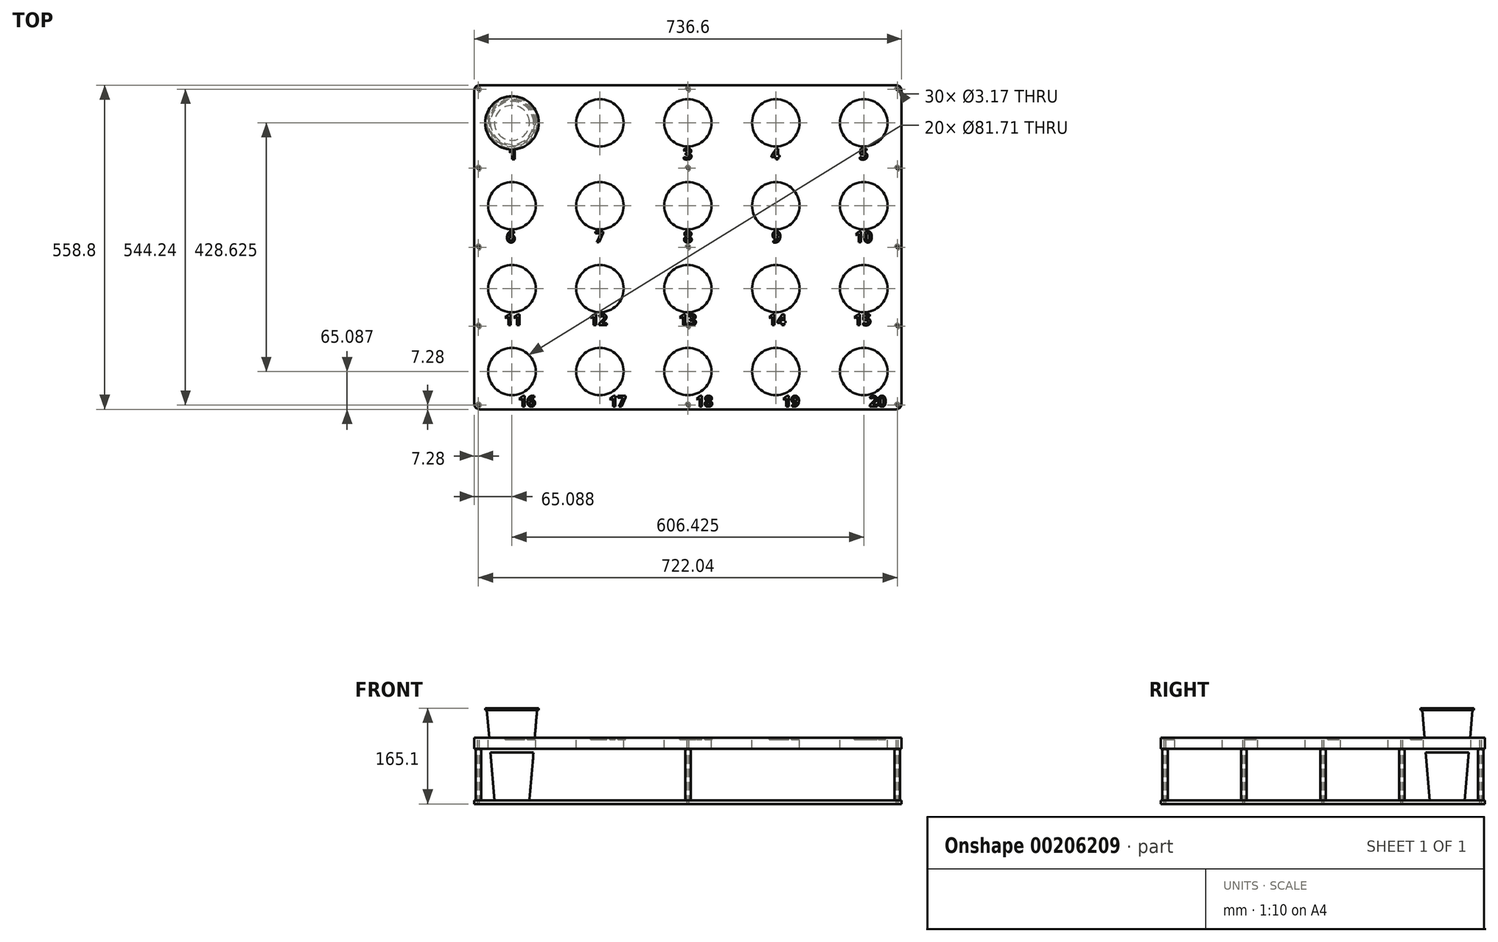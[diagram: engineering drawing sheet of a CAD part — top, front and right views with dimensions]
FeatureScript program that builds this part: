
annotation { "Feature Type Name" : "Feature", "Feature Type Description" : "" }
export const myFeature = defineFeature(function(context is Context, id is Id, definition is map)
    precondition{}
    {
        {
            var Q0;
            Q0=qCreatedBy(makeId("Top.planeOp"),FACE);
            var sketch = newSketch(context, id + "F0", { "sketchPlane" : qUnion([Q0])});
            skLineSegment(sketch, "E0.bottom", {"start": v(368.3, -279.4) * mm, "end": v(-368.3, -279.4) * mm});
            skLineSegment(sketch, "E0.top", {"start": v(368.3, 279.4) * mm, "end": v(-368.3, 279.4) * mm});
            skLineSegment(sketch, "E0.left", {"start": v(368.3, -279.4) * mm, "end": v(368.3, 279.4) * mm});
            skLineSegment(sketch, "E0.right", {"start": v(-368.3, -279.4) * mm, "end": v(-368.3, 279.4) * mm});
            skPoint(sketch, "E0.middle", {"position": v(0, 0) * mm});
            skSolve(sketch);
        }
        {
            var Q0;
            Q0 = qSketchRegion(id + "F0", true);
            extrude(context, id + "F1", {"entities" : qUnion([Q0]), "oppositeDirection" : true, "depth" : 19.05 * mm});
        }
        {
            var Q0;
            Q0=makeQuery(id+"F1.opExtrude","SWEPT_EDGE",EDGE,{"disambiguationData":[OSD([sQuery(id+"F0.wireOp",EDGE,"E0.bottom"),sQuery(id+"F0.wireOp",EDGE,"E0.right")])]});
            var Q1;
            Q1=makeQuery(id+"F1.opExtrude","SWEPT_EDGE",EDGE,{"disambiguationData":[OSD([sQuery(id+"F0.wireOp",EDGE,"E0.bottom"),sQuery(id+"F0.wireOp",EDGE,"E0.left")])]});
            var Q2;
            Q2=makeQuery(id+"F1.opExtrude","SWEPT_EDGE",EDGE,{"disambiguationData":[OSD([sQuery(id+"F0.wireOp",EDGE,"E0.top"),sQuery(id+"F0.wireOp",EDGE,"E0.left")])]});
            var Q3;
            Q3=makeQuery(id+"F1.opExtrude","SWEPT_EDGE",EDGE,{"disambiguationData":[OSD([sQuery(id+"F0.wireOp",EDGE,"E0.top"),sQuery(id+"F0.wireOp",EDGE,"E0.right")])]});
            fillet(context, id + "F2", {"entities" : qUnion([Q0, Q1, Q2, Q3]), "radius" : 9.52 * mm, "tangentPropagation" : true, "allowEdgeOverflow" : false});
        }
        {
            var Q0;
            Q0=makeQuery(id+"F1.opExtrude","CAP_FACE",FACE,{"disambiguationData":[OSD([sQuery(id+"F0.wireOp",EDGE,"E0.bottom"),sQuery(id+"F0.wireOp",EDGE,"E0.top"),sQuery(id+"F0.wireOp",EDGE,"E0.left"),sQuery(id+"F0.wireOp",EDGE,"E0.right")])],"isStart":false});
            var sketch = newSketch(context, id + "F3", { "sketchPlane" : qUnion([Q0])});
            skCircle(sketch, "E1", {"center": v(-361.02, 272.12) * mm, "radius": 4.76 * mm});
            skCircle(sketch, "E2", {"center": v(-361.02, 272.12) * mm, "radius": 6.35 * mm, "construction": true});
            skLineSegment(sketch, "E3", {"start": v(-361.02, 272.12) * mm, "end": v(-368.3, 272.12) * mm, "construction": true});
            skLineSegment(sketch, "E4", {"start": v(-361.02, 272.12) * mm, "end": v(-361.02, 279.4) * mm, "construction": true});
            skLineSegment(sketch, "E5", {"start": v(0, 0) * mm, "end": v(-361.02, 0) * mm, "construction": true});
            skLineSegment(sketch, "E6", {"start": v(0, 0) * mm, "end": v(0, 189.11) * mm, "construction": true});
            skLineSegment(sketch, "E7", {"start": v(-361.02, 272.12) * mm, "end": v(-361.02, 136.06) * mm, "construction": true});
            skLineSegment(sketch, "E8", {"start": v(-361.02, 136.06) * mm, "end": v(-361.02, 0) * mm, "construction": true});
            skCircle(sketch, "E9", {"center": v(-361.02, 136.06) * mm, "radius": 4.76 * mm});
            skCircle(sketch, "E10", {"center": v(-361.02, 0) * mm, "radius": 4.76 * mm});
            skCircle(sketch, "E11.MirrorC", {"center": v(-361.02, -136.06) * mm, "radius": 4.76 * mm});
            skCircle(sketch, "E12.MirrorC", {"center": v(-361.02, -272.12) * mm, "radius": 4.76 * mm});
            skCircle(sketch, "E13.MirrorC", {"center": v(361.02, -272.12) * mm, "radius": 4.76 * mm});
            skCircle(sketch, "E14.MirrorC", {"center": v(361.02, -136.06) * mm, "radius": 4.76 * mm});
            skCircle(sketch, "E15.MirrorC", {"center": v(361.02, 0) * mm, "radius": 4.76 * mm});
            skCircle(sketch, "E16.MirrorC", {"center": v(361.02, 136.06) * mm, "radius": 4.76 * mm});
            skCircle(sketch, "E17.MirrorC", {"center": v(361.02, 272.12) * mm, "radius": 4.76 * mm});
            skCircle(sketch, "E18.1.0.0", {"center": v(0, 272.12) * mm, "radius": 4.76 * mm});
            skCircle(sketch, "E18.1.0.1", {"center": v(0, 136.06) * mm, "radius": 4.76 * mm});
            skCircle(sketch, "E18.1.0.2", {"center": v(0, 0) * mm, "radius": 4.76 * mm});
            skCircle(sketch, "E18.1.0.3", {"center": v(0, -136.06) * mm, "radius": 4.76 * mm});
            skCircle(sketch, "E18.1.0.4", {"center": v(0, -272.12) * mm, "radius": 4.76 * mm});
            skLineSegment(sketch, "E18.direction1", {"start": v(-361.02, 272.12) * mm, "end": v(0, 272.12) * mm, "construction": true});
            skSolve(sketch);
        }
        {
            var Q0;
            Q0 = qSketchRegion(id + "F3", true);
            extrude(context, id + "F4", {"entities" : qUnion([Q0]), "depth" : 88.9 * mm});
        }
        {
            var Q0;
            Q0=makeQuery(id+"F4.opExtrude","CAP_FACE",FACE,{"disambiguationData":[OSD([sQuery(id+"F3.wireOp",EDGE,"E12.MirrorC")])],"isStart":false});
            var sketch = newSketch(context, id + "F5", { "sketchPlane" : qUnion([Q0])});
            skLineSegment(sketch, "E19.0.0", {"start": v(-358.78, 279.4) * mm, "end": v(358.77, 279.4) * mm});
            skArc(sketch, "E19.0.1", {"start": v(358.77, 279.4) * mm, "mid": v(365.51, 276.61) * mm, "end": v(368.3, 269.88) * mm});
            skLineSegment(sketch, "E19.0.2", {"start": v(368.3, 269.88) * mm, "end": v(368.3, -269.88) * mm});
            skArc(sketch, "E19.0.3", {"start": v(368.3, -269.88) * mm, "mid": v(365.51, -276.61) * mm, "end": v(358.78, -279.4) * mm});
            skLineSegment(sketch, "E19.0.4", {"start": v(358.78, -279.4) * mm, "end": v(-358.77, -279.4) * mm});
            skArc(sketch, "E19.0.5", {"start": v(-358.77, -279.4) * mm, "mid": v(-365.51, -276.61) * mm, "end": v(-368.3, -269.88) * mm});
            skLineSegment(sketch, "E19.0.6", {"start": v(-368.3, -269.88) * mm, "end": v(-368.3, 269.88) * mm});
            skArc(sketch, "E19.0.7", {"start": v(-368.3, 269.88) * mm, "mid": v(-365.51, 276.61) * mm, "end": v(-358.78, 279.4) * mm});
            skSolve(sketch);
        }
        {
            var Q0;
            Q0 = qSketchRegion(id + "F5", true);
            extrude(context, id + "F6", {"entities" : qUnion([Q0]), "operationType" : NewBodyOperationType.ADD, "depth" : 6.35 * mm});
        }
        {
            var Q0;
            Q0=makeQuery(id+"F1.opExtrude","CAP_FACE",FACE,{"disambiguationData":[OSD([sQuery(id+"F0.wireOp",EDGE,"E0.bottom"),sQuery(id+"F0.wireOp",EDGE,"E0.top"),sQuery(id+"F0.wireOp",EDGE,"E0.left"),sQuery(id+"F0.wireOp",EDGE,"E0.right")])],"isStart":true});
            var sketch = newSketch(context, id + "F7", { "sketchPlane" : qUnion([Q0])});
            skCircle(sketch, "E20", {"center": v(-303.21, 214.31) * mm, "radius": 46.04 * mm});
            skCircle(sketch, "E21.0.1.0", {"center": v(-303.21, 71.44) * mm, "radius": 46.04 * mm});
            skCircle(sketch, "E21.0.2.0", {"center": v(-303.21, -71.44) * mm, "radius": 46.04 * mm});
            skCircle(sketch, "E21.0.3.0", {"center": v(-303.21, -214.31) * mm, "radius": 46.04 * mm});
            skCircle(sketch, "E21.1.0.0", {"center": v(-151.6, 214.31) * mm, "radius": 46.04 * mm});
            skCircle(sketch, "E21.1.1.0", {"center": v(-151.6, 71.44) * mm, "radius": 46.04 * mm});
            skCircle(sketch, "E21.1.2.0", {"center": v(-151.6, -71.44) * mm, "radius": 46.04 * mm});
            skCircle(sketch, "E21.1.3.0", {"center": v(-151.6, -214.31) * mm, "radius": 46.04 * mm});
            skCircle(sketch, "E21.2.0.0", {"center": v(0, 214.31) * mm, "radius": 46.04 * mm});
            skCircle(sketch, "E21.2.1.0", {"center": v(0, 71.44) * mm, "radius": 46.04 * mm});
            skCircle(sketch, "E21.2.2.0", {"center": v(0, -71.44) * mm, "radius": 46.04 * mm});
            skCircle(sketch, "E21.2.3.0", {"center": v(0, -214.31) * mm, "radius": 46.04 * mm});
            skCircle(sketch, "E21.3.0.0", {"center": v(151.6, 214.31) * mm, "radius": 46.04 * mm});
            skCircle(sketch, "E21.3.1.0", {"center": v(151.6, 71.44) * mm, "radius": 46.04 * mm});
            skCircle(sketch, "E21.3.2.0", {"center": v(151.6, -71.44) * mm, "radius": 46.04 * mm});
            skCircle(sketch, "E21.3.3.0", {"center": v(151.6, -214.31) * mm, "radius": 46.04 * mm});
            skCircle(sketch, "E21.4.0.0", {"center": v(303.21, 214.31) * mm, "radius": 46.04 * mm});
            skCircle(sketch, "E21.4.1.0", {"center": v(303.21, 71.44) * mm, "radius": 46.04 * mm});
            skCircle(sketch, "E21.4.2.0", {"center": v(303.21, -71.44) * mm, "radius": 46.04 * mm});
            skCircle(sketch, "E21.4.3.0", {"center": v(303.21, -214.31) * mm, "radius": 46.04 * mm});
            skLineSegment(sketch, "E21.direction1", {"start": v(-303.21, 214.31) * mm, "end": v(-151.6, 214.31) * mm, "construction": true});
            skLineSegment(sketch, "E21.direction2", {"start": v(-303.21, 71.44) * mm, "end": v(-303.21, 214.31) * mm, "construction": true});
            skSolve(sketch);
        }
        {
            var Q0;
            Q0=makeQuery(id+"F6.opExtrude","CAP_FACE",FACE,{"disambiguationData":[OSD([sQuery(id+"F5.wireOp",EDGE,"E19.0.0"),sQuery(id+"F5.wireOp",EDGE,"E19.0.1"),sQuery(id+"F5.wireOp",EDGE,"E19.0.2"),sQuery(id+"F5.wireOp",EDGE,"E19.0.3"),sQuery(id+"F5.wireOp",EDGE,"E19.0.4"),sQuery(id+"F5.wireOp",EDGE,"E19.0.5"),sQuery(id+"F5.wireOp",EDGE,"E19.0.6"),sQuery(id+"F5.wireOp",EDGE,"E19.0.7")])],"isStart":true});
            var sketch = newSketch(context, id + "F8", { "sketchPlane" : qUnion([Q0])});
            skCircle(sketch, "E22", {"center": v(-303.21, 214.31) * mm, "radius": 30.16 * mm});
            skSolve(sketch);
        }
        {
            var Q0;
            Q0=makeQuery(id+"F8.imprint","IMPRINT",FACE,{"disambiguationData":[TD([[makeQuery(id+"F8.imprint","IMPRINT",EDGE,{"derivedFrom":sQuery(id+"F8.wireOp",EDGE,"E22")}),-1.0]])]});
            cPlane(context, id + "F9", {"entities" : qUnion([Q0]), "cplaneType" : CPlaneType.OFFSET, "offset" : 155.57 * mm, "width" : 152.4 * mm, "height" : 152.4 * mm});
        }
        {
            var Q0;
            Q0=qCreatedBy(id+"F9.planeOp",FACE);
            var sketch = newSketch(context, id + "F10", { "sketchPlane" : qUnion([Q0])});
            skCircle(sketch, "E23", {"center": v(-303.21, 214.31) * mm, "radius": 43.28 * mm});
            skSolve(sketch);
        }
        {
            var Q0;
            Q0=makeQuery(id+"F10.imprint","IMPRINT",FACE,{"disambiguationData":[TD([[makeQuery(id+"F10.imprint","IMPRINT",EDGE,{"derivedFrom":sQuery(id+"F10.wireOp",EDGE,"E23")}),1.0]])]});
            var Q1;
            Q1 = qSketchRegion(id + "F8", true);
            loft(context, id + "F11", {"sheetProfilesArray" : [{ "sheetProfileEntities" : qUnion([Q0]) }, { "sheetProfileEntities" : qUnion([Q1]) }]});
        }
        {
            var Q0;
            Q0=makeQuery(id+"F11.opLoft","CAP_FACE",FACE,{"disambiguationData":[OSD([makeQuery(id+"F10.imprint","IMPRINT",FACE,{"disambiguationData":[TD([[makeQuery(id+"F10.imprint","IMPRINT",EDGE,{"derivedFrom":sQuery(id+"F10.wireOp",EDGE,"E23")}),1.0]])]})])],"isStart":true});
            var sketch = newSketch(context, id + "F12", { "sketchPlane" : qUnion([Q0])});
            skCircle(sketch, "E24", {"center": v(-303.21, 214.31) * mm, "radius": 46.04 * mm});
            skSolve(sketch);
        }
        {
            var Q0;
            Q0 = qSketchRegion(id + "F12", true);
            extrude(context, id + "F13", {"entities" : qUnion([Q0]), "operationType" : NewBodyOperationType.ADD, "depth" : 3.17 * mm});
        }
        {
            var Q0;
            Q0=makeQuery(id+"F1.opExtrude","CAP_FACE",FACE,{"disambiguationData":[OSD([sQuery(id+"F0.wireOp",EDGE,"E0.bottom"),sQuery(id+"F0.wireOp",EDGE,"E0.top"),sQuery(id+"F0.wireOp",EDGE,"E0.left"),sQuery(id+"F0.wireOp",EDGE,"E0.right")])],"isStart":true});
            var sketch = newSketch(context, id + "F14", { "sketchPlane" : qUnion([Q0])});
            skCircle(sketch, "E25", {"center": v(-303.21, 214.31) * mm, "radius": 39.27 * mm, "construction": true});
            skCircle(sketch, "E26.0", {"center": v(-303.21, 214.31) * mm, "radius": 40.85 * mm});
            skCircle(sketch, "E27.0.1.0", {"center": v(-303.21, 71.44) * mm, "radius": 40.85 * mm});
            skCircle(sketch, "E27.0.2.0", {"center": v(-303.21, -71.44) * mm, "radius": 40.85 * mm});
            skCircle(sketch, "E27.0.3.0", {"center": v(-303.21, -214.31) * mm, "radius": 40.85 * mm});
            skCircle(sketch, "E27.1.0.0", {"center": v(-151.6, 214.31) * mm, "radius": 40.85 * mm});
            skCircle(sketch, "E27.1.1.0", {"center": v(-151.6, 71.44) * mm, "radius": 40.85 * mm});
            skCircle(sketch, "E27.1.2.0", {"center": v(-151.6, -71.44) * mm, "radius": 40.85 * mm});
            skCircle(sketch, "E27.1.3.0", {"center": v(-151.6, -214.31) * mm, "radius": 40.85 * mm});
            skCircle(sketch, "E27.2.0.0", {"center": v(0, 214.31) * mm, "radius": 40.85 * mm});
            skCircle(sketch, "E27.2.1.0", {"center": v(0, 71.44) * mm, "radius": 40.85 * mm});
            skCircle(sketch, "E27.2.2.0", {"center": v(0, -71.44) * mm, "radius": 40.85 * mm});
            skCircle(sketch, "E27.2.3.0", {"center": v(0, -214.31) * mm, "radius": 40.85 * mm});
            skCircle(sketch, "E27.3.0.0", {"center": v(151.6, 214.31) * mm, "radius": 40.85 * mm});
            skCircle(sketch, "E27.3.1.0", {"center": v(151.6, 71.44) * mm, "radius": 40.85 * mm});
            skCircle(sketch, "E27.3.2.0", {"center": v(151.6, -71.44) * mm, "radius": 40.85 * mm});
            skCircle(sketch, "E27.3.3.0", {"center": v(151.6, -214.31) * mm, "radius": 40.85 * mm});
            skCircle(sketch, "E27.4.0.0", {"center": v(303.21, 214.31) * mm, "radius": 40.85 * mm});
            skCircle(sketch, "E27.4.1.0", {"center": v(303.21, 71.44) * mm, "radius": 40.85 * mm});
            skCircle(sketch, "E27.4.2.0", {"center": v(303.21, -71.44) * mm, "radius": 40.85 * mm});
            skCircle(sketch, "E27.4.3.0", {"center": v(303.21, -214.31) * mm, "radius": 40.85 * mm});
            skLineSegment(sketch, "E27.direction1", {"start": v(-303.21, 214.31) * mm, "end": v(-151.6, 214.31) * mm, "construction": true});
            skLineSegment(sketch, "E27.direction2", {"start": v(-303.21, 71.44) * mm, "end": v(-303.21, 214.31) * mm, "construction": true});
            skSolve(sketch);
        }
        {
            var Q0;
            Q0 = qSketchRegion(id + "F14", true);
            extrude(context, id + "F15", {"entities" : qUnion([Q0]), "operationType" : NewBodyOperationType.REMOVE, "oppositeDirection" : true, "depth" : 25.4 * mm});
        }
        {
            var Q0;
            Q0=makeQuery(id+"F1.opExtrude","CAP_FACE",FACE,{"disambiguationData":[OSD([sQuery(id+"F0.wireOp",EDGE,"E0.bottom"),sQuery(id+"F0.wireOp",EDGE,"E0.top"),sQuery(id+"F0.wireOp",EDGE,"E0.left"),sQuery(id+"F0.wireOp",EDGE,"E0.right")])],"isStart":true});
            var sketch = newSketch(context, id + "F16", { "sketchPlane" : qUnion([Q0])});
            skPoint(sketch, "E28", {"position": v(-303.21, 214.31) * mm});
            skPoint(sketch, "E29", {"position": v(-151.6, 214.31) * mm});
            skPoint(sketch, "E30", {"position": v(0, 214.31) * mm});
            skPoint(sketch, "E31", {"position": v(151.6, 214.31) * mm});
            skPoint(sketch, "E32", {"position": v(303.21, 214.31) * mm});
            skPoint(sketch, "E33", {"position": v(-303.21, -71.44) * mm});
            skPoint(sketch, "E34", {"position": v(-303.21, -214.31) * mm});
            skPoint(sketch, "E35", {"position": v(-303.21, 71.44) * mm});
            skText(sketch, "E36", { "text": "1", "fontName": "OpenSans-Bold.ttf"});
            skText(sketch, "E37", { "text": "3", "fontName": "OpenSans-Bold.ttf"});
            skText(sketch, "E38", { "text": "4", "fontName": "OpenSans-Bold.ttf"});
            skText(sketch, "E39", { "text": "5", "fontName": "OpenSans-Bold.ttf"});
            skText(sketch, "E40", { "text": "6                    7                    8                    9", "fontName": "OpenSans-Bold.ttf"});
            skPoint(sketch, "E41", {"position": v(151.6, 71.44) * mm});
            skLineSegment(sketch, "E42", {"start": v(-303.21, 71.44) * mm, "end": v(151.6, 71.44) * mm, "construction": true});
            skLineSegment(sketch, "E43", {"start": v(-75.8, 71.44) * mm, "end": v(-75.8, 27.4) * mm, "construction": true});
            skText(sketch, "E44", { "text": "10\n", "fontName": "OpenSans-Bold.ttf"});
            skPoint(sketch, "E45", {"position": v(303.21, 71.44) * mm});
            skText(sketch, "E46", { "text": "11                 12                  13                  14                 15", "fontName": "OpenSans-Bold.ttf"});
            skText(sketch, "E47", { "text": "16                   17                  18                  19                  20", "fontName": "OpenSans-Bold.ttf"});
            const initialGuessF16  = {"E36": [-0.30954, 0.15123, 1, 0, 0.01905], "E37": [-0.0079, 0.15123, 1, 0, 0.01905], "E38": [0.1434, 0.15123, 1, 0, 0.01905], "E39": [0.2954, 0.15123, 1, 0, 0.01905], "E40": [-0.31266, 0.00836, 1, 0, 0.01905], "E44": [0.28772, 0.00836, 1, 0, 0.01905], "E46": [-0.3164, -0.13452, 1, 0, 0.01905], "E47": [-0.2921, -0.27464, 1, 0, 0.0185]};
            skSetInitialGuess(sketch, initialGuessF16);
            skSolve(sketch);
        }
        {
            var Q0;
            Q0 = qSketchRegion(id + "F16", true);
            extrude(context, id + "F17", {"entities" : qUnion([Q0]), "operationType" : NewBodyOperationType.REMOVE, "oppositeDirection" : true, "depth" : 3.3 * mm});
        }
        {
            var Q0;
            {var subQ0=sQuery(id+"F0.wireOp",EDGE,"E0.left");var subQ1=sQuery(id+"F0.wireOp",EDGE,"E0.top");var subQ2=sQuery(id+"F0.wireOp",EDGE,"E0.right");var subQ3=sQuery(id+"F0.wireOp",EDGE,"E0.bottom");Q0=makeQuery(id+"F17.boolean.opBoolean","SPLIT",FACE,{"disambiguationData":[TD([makeQuery(id+"F1.opExtrude","SWEPT_FACE",FACE,{"disambiguationData":[OSD([subQ3])]})])],"derivedFrom":makeQuery(id+"F1.opExtrude","CAP_FACE",FACE,{"disambiguationData":[OSD([subQ3,subQ1,subQ0,subQ2])],"isStart":true})});}
            var sketch = newSketch(context, id + "F18", { "sketchPlane" : qUnion([Q0])});
            skCircle(sketch, "E48", {"center": v(-361.02, 272.12) * mm, "radius": 1.59 * mm});
            skCircle(sketch, "E49.0.1.0", {"center": v(-361.02, 136.06) * mm, "radius": 1.59 * mm});
            skCircle(sketch, "E49.0.2.0", {"center": v(-361.02, 0) * mm, "radius": 1.59 * mm});
            skCircle(sketch, "E49.0.3.0", {"center": v(-361.02, -136.06) * mm, "radius": 1.59 * mm});
            skCircle(sketch, "E49.0.4.0", {"center": v(-361.02, -272.12) * mm, "radius": 1.59 * mm});
            skCircle(sketch, "E49.1.0.0", {"center": v(0, 272.12) * mm, "radius": 1.59 * mm});
            skCircle(sketch, "E49.1.1.0", {"center": v(0, 136.06) * mm, "radius": 1.59 * mm});
            skCircle(sketch, "E49.1.2.0", {"center": v(0, 0) * mm, "radius": 1.59 * mm});
            skCircle(sketch, "E49.1.3.0", {"center": v(0, -136.06) * mm, "radius": 1.59 * mm});
            skCircle(sketch, "E49.1.4.0", {"center": v(0, -272.12) * mm, "radius": 1.59 * mm});
            skCircle(sketch, "E49.2.0.0", {"center": v(361.02, 272.12) * mm, "radius": 1.59 * mm});
            skCircle(sketch, "E49.2.1.0", {"center": v(361.02, 136.06) * mm, "radius": 1.59 * mm});
            skCircle(sketch, "E49.2.2.0", {"center": v(361.02, 0) * mm, "radius": 1.59 * mm});
            skCircle(sketch, "E49.2.3.0", {"center": v(361.02, -136.06) * mm, "radius": 1.59 * mm});
            skCircle(sketch, "E49.2.4.0", {"center": v(361.02, -272.12) * mm, "radius": 1.59 * mm});
            skLineSegment(sketch, "E49.direction1", {"start": v(-361.02, 272.12) * mm, "end": v(0, 272.12) * mm, "construction": true});
            skLineSegment(sketch, "E49.direction2", {"start": v(-361.02, 136.06) * mm, "end": v(-361.02, 272.12) * mm, "construction": true});
            skSolve(sketch);
        }
        {
            var Q0;
            Q0 = qSketchRegion(id + "F18", true);
            extrude(context, id + "F19", {"entities" : qUnion([Q0]), "operationType" : NewBodyOperationType.REMOVE, "endBound" : BoundingType.THROUGH_ALL, "oppositeDirection" : true, "depth" : 25.4 * mm});
        }
    });
